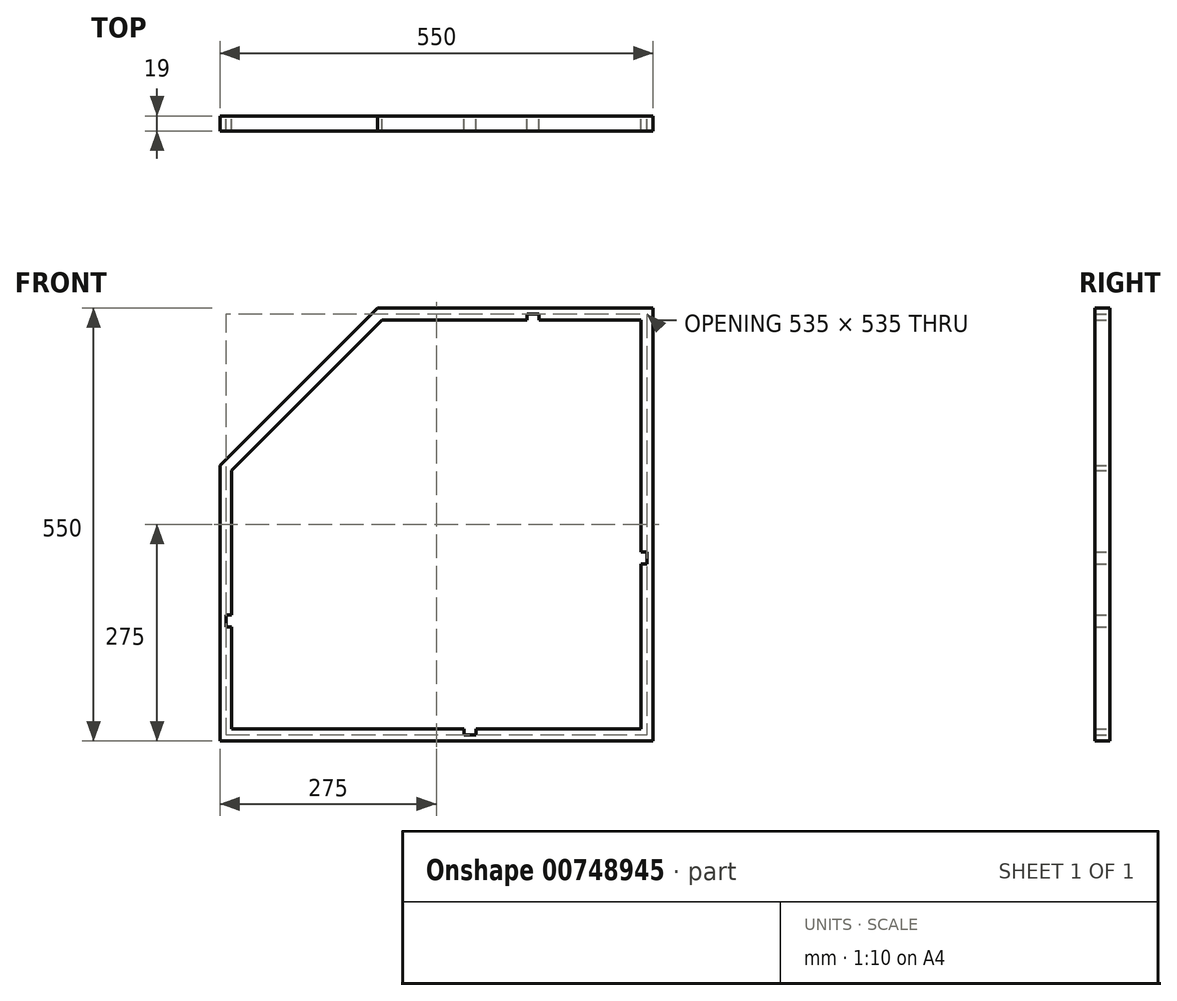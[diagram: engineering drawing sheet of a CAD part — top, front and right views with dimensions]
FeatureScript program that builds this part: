
annotation { "Feature Type Name" : "Feature", "Feature Type Description" : "" }
export const myFeature = defineFeature(function(context is Context, id is Id, definition is map)
    precondition{}
    {
        {
            var Q0;
            Q0=qCreatedBy(makeId("Front.planeOp"),FACE);
            var sketch = newSketch(context, id + "F0", { "sketchPlane" : qUnion([Q0])});
            skLineSegment(sketch, "E0.top", {"start": v(-275, -275) * mm, "end": v(275, -275) * mm});
            skLineSegment(sketch, "E0.right", {"start": v(275, 275) * mm, "end": v(275, -275) * mm});
            skPoint(sketch, "E0.middle", {"position": v(0, 0) * mm});
            skLineSegment(sketch, "E1", {"start": v(-75, 275) * mm, "end": v(275, 275) * mm});
            skLineSegment(sketch, "E2", {"start": v(-275, -275) * mm, "end": v(-275, 75) * mm});
            skLineSegment(sketch, "E3", {"start": v(275, 275) * mm, "end": v(-75, 275) * mm});
            skLineSegment(sketch, "E4", {"start": v(-75, 275) * mm, "end": v(-275, 75) * mm});
            skPoint(sketch, "E5.orphan", {"position": v(-275, 275) * mm});
            skLineSegment(sketch, "E6.0", {"start": v(-260, -260) * mm, "end": v(-260, -130) * mm});
            skLineSegment(sketch, "E6.1", {"start": v(-68.79, 260) * mm, "end": v(-260, 68.79) * mm});
            skLineSegment(sketch, "E6.2", {"start": v(-260, -260) * mm, "end": v(35, -260) * mm});
            skLineSegment(sketch, "E6.3", {"start": v(260, 260) * mm, "end": v(260, -35) * mm});
            skLineSegment(sketch, "E6.4", {"start": v(260, 260) * mm, "end": v(130, 260) * mm});
            skLineSegment(sketch, "E7", {"start": v(-275, 275) * mm, "end": v(-175, 175) * mm, "construction": true});
            skLineSegment(sketch, "E8.trimOffspring", {"start": v(275, -275) * mm, "end": v(391.98, -391.98) * mm, "construction": true});
            skLineSegment(sketch, "E9", {"start": v(260, -260) * mm, "end": v(47.8, -47.8) * mm, "construction": true});
            skCircle(sketch, "E10", {"center": v(153.9, -153.9) * mm, "radius": 65 * mm, "construction": true});
            skCircle(sketch, "E11", {"center": v(-58.3, 58.3) * mm, "radius": 65 * mm, "construction": true});
            skLineSegment(sketch, "E12.bottom", {"start": v(260, -50) * mm, "end": v(267.5, -50) * mm});
            skLineSegment(sketch, "E12.top", {"start": v(260, -35) * mm, "end": v(267.5, -35) * mm});
            skLineSegment(sketch, "E12.right", {"start": v(267.5, -50) * mm, "end": v(267.5, -35) * mm});
            skLineSegment(sketch, "E13.trimOffspring", {"start": v(260, -50) * mm, "end": v(260, -260) * mm});
            skLineSegment(sketch, "E14", {"start": v(260, -35) * mm, "end": v(130, -35) * mm});
            skLineSegment(sketch, "E15", {"start": v(130, 260) * mm, "end": v(130, -35) * mm});
            skLineSegment(sketch, "E16.0", {"start": v(260, -50) * mm, "end": v(115, -50) * mm});
            skLineSegment(sketch, "E17.MirrorCS", {"start": v(-260, -115) * mm, "end": v(50, -115) * mm});
            skLineSegment(sketch, "E18.MirrorCS", {"start": v(-260, -130) * mm, "end": v(35, -130) * mm});
            skLineSegment(sketch, "E19.MirrorCS", {"start": v(50, -260) * mm, "end": v(50, -115) * mm});
            skLineSegment(sketch, "E20.MirrorCS", {"start": v(35, -260) * mm, "end": v(35, -130) * mm});
            skLineSegment(sketch, "E21.MirrorCS", {"start": v(35, -260) * mm, "end": v(35, -267.5) * mm});
            skLineSegment(sketch, "E22.MirrorCS", {"start": v(50, -260) * mm, "end": v(50, -267.5) * mm});
            skLineSegment(sketch, "E23.MirrorCS", {"start": v(50, -267.5) * mm, "end": v(35, -267.5) * mm});
            skLineSegment(sketch, "E24.trimOffspring", {"start": v(50, -260) * mm, "end": v(260, -260) * mm});
            skLineSegment(sketch, "E25.bottom", {"start": v(-260, -130) * mm, "end": v(-267.5, -130) * mm});
            skLineSegment(sketch, "E25.top", {"start": v(-260, -115) * mm, "end": v(-267.5, -115) * mm});
            skLineSegment(sketch, "E25.right", {"start": v(-267.5, -130) * mm, "end": v(-267.5, -115) * mm});
            skLineSegment(sketch, "E26.trimOffspring", {"start": v(-260, -115) * mm, "end": v(-260, 68.79) * mm});
            skLineSegment(sketch, "E27.top", {"start": v(130, 267.5) * mm, "end": v(115, 267.5) * mm});
            skLineSegment(sketch, "E27.left", {"start": v(130, 260) * mm, "end": v(130, 267.5) * mm});
            skLineSegment(sketch, "E27.right", {"start": v(115, 260) * mm, "end": v(115, 267.5) * mm});
            skLineSegment(sketch, "E28.trimOffspring", {"start": v(115, 260) * mm, "end": v(-68.79, 260) * mm});
            skLineSegment(sketch, "E29", {"start": v(50, -115) * mm, "end": v(115, -50) * mm});
            skLineSegment(sketch, "E30", {"start": v(28.79, -115) * mm, "end": v(50, -115) * mm});
            skLineSegment(sketch, "E31", {"start": v(115, -50) * mm, "end": v(115, 260) * mm});
            skLineSegment(sketch, "E32", {"start": v(28.79, -115) * mm, "end": v(115, -28.79) * mm});
            skLineSegment(sketch, "E33", {"start": v(115, -28.79) * mm, "end": v(115, -50) * mm});
            skLineSegment(sketch, "E34", {"start": v(-260, -115) * mm, "end": v(115, 260) * mm});
            skLineSegment(sketch, "E35.0", {"start": v(-238.79, -115) * mm, "end": v(115, 238.79) * mm});
            skLineSegment(sketch, "E36", {"start": v(-260, -115) * mm, "end": v(-238.79, -115) * mm});
            skLineSegment(sketch, "E37", {"start": v(115, 238.79) * mm, "end": v(115, 260) * mm});
            skLineSegment(sketch, "E38", {"start": v(24.98, -26.89) * mm, "end": v(-63.14, -115) * mm});
            skLineSegment(sketch, "E39", {"start": v(24.98, -26.89) * mm, "end": v(115, 63.14) * mm});
            skLineSegment(sketch, "E40", {"start": v(35.58, -37.5) * mm, "end": v(-41.92, -115) * mm});
            skLineSegment(sketch, "E41", {"start": v(35.58, -37.5) * mm, "end": v(115, 41.92) * mm});
            skSolve(sketch);
        }
        {
            var Q0;
            Q0=qSketchRegion(id+"F0",true);
            extrude(context, id + "F1", {"entities" : qUnion([Q0]), "depth" : 19 * mm, "offsetDistance" : 25 * mm, "symmetric" : true});
        }
    });
